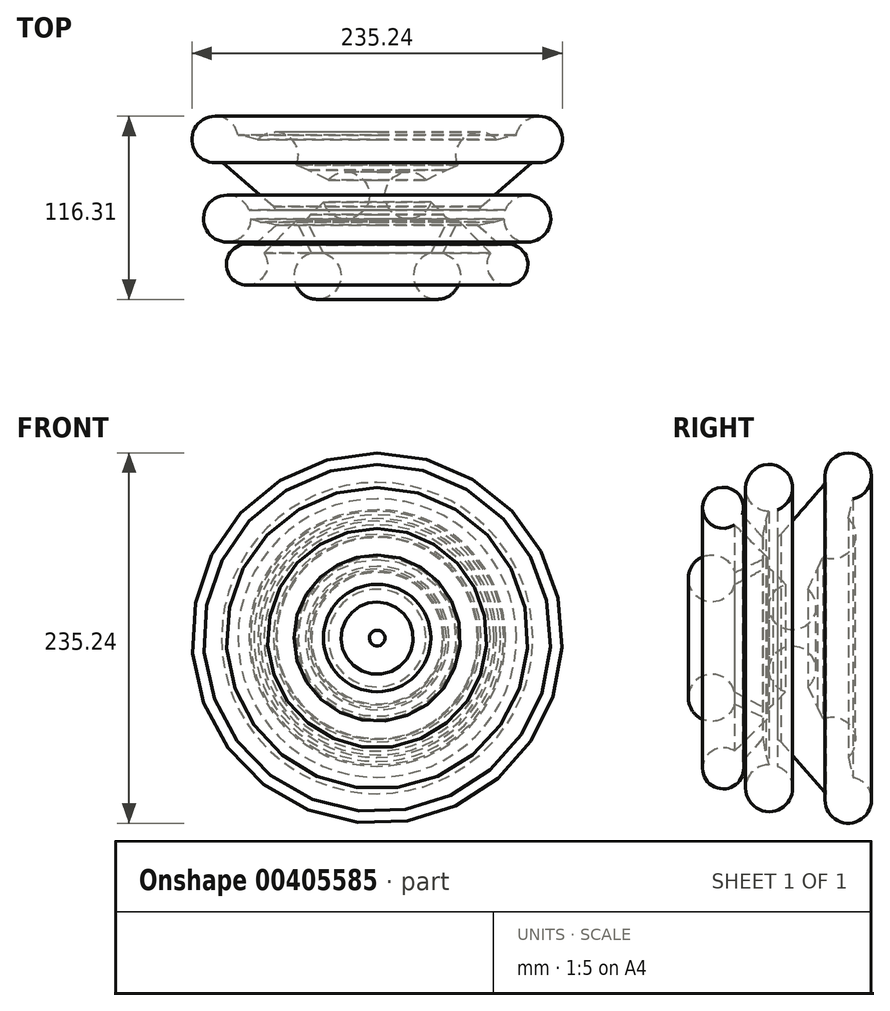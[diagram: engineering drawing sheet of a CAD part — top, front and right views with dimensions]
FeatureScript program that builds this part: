
annotation { "Feature Type Name" : "Feature", "Feature Type Description" : "" }
export const myFeature = defineFeature(function(context is Context, id is Id, definition is map)
    precondition{}
    {
        {
            var Q0;
            Q0=qCreatedBy(makeId("Top.planeOp"),FACE);
            var sketch = newSketch(context, id + "F0", { "sketchPlane" : qUnion([Q0])});
            skCircle(sketch, "E0", {"center": v(0, 48.43) * mm, "radius": 14.9 * mm});
            skCircle(sketch, "E1", {"center": v(-45.12, 23.16) * mm, "radius": 14.86 * mm});
            skCircle(sketch, "E2", {"center": v(-27.07, -27.97) * mm, "radius": 14.93 * mm});
            skCircle(sketch, "E3", {"center": v(17.75, -20.76) * mm, "radius": 13.06 * mm});
            skCircle(sketch, "E4", {"center": v(30.38, 8.42) * mm, "radius": 14.91 * mm});
            skCircle(sketch, "E5", {"center": v(37.9, 58.65) * mm, "radius": 14.75 * mm});
            skEllipticalArc(sketch, "E6", {});
            skEllipticalArc(sketch, "E7", {});
            skEllipticalArc(sketch, "E8.trimOffspring", {});
            skEllipticalArc(sketch, "E9.trimOffspring", {});
            skLineSegment(sketch, "E10", {"start": v(-34.02, 33.04) * mm, "end": v(-21.06, 39.1) * mm});
            skPoint(sketch, "E10.endSnap0", {"position": v(-21.06, 27.67) * mm});
            skLineSegment(sketch, "E11", {"start": v(-21.06, 39.1) * mm, "end": v(-13.65, 42.47) * mm});
            skLineSegment(sketch, "E12", {"start": v(-13.65, 42.47) * mm, "end": v(-11.61, 39.1) * mm});
            skLineSegment(sketch, "E13", {"start": v(-11.61, 39.1) * mm, "end": v(-30.9, 27.44) * mm});
            skLineSegment(sketch, "E14", {"start": v(-30.9, 27.44) * mm, "end": v(-19.47, 19.73) * mm});
            skLineSegment(sketch, "E15", {"start": v(-30.9, 18.88) * mm, "end": v(-22.56, 10.83) * mm});
            skLineSegment(sketch, "E16", {"start": v(-19.47, 8) * mm, "end": v(-30.9, -13.54) * mm});
            skLineSegment(sketch, "E17", {"start": v(-23.25, -13.54) * mm, "end": v(-13.65, 7.26) * mm});
            skLineSegment(sketch, "E18", {"start": v(-13.65, 7.26) * mm, "end": v(6.86, -13.54) * mm});
            skLineSegment(sketch, "E19", {"start": v(13.37, -8.45) * mm, "end": v(0, 3.3) * mm});
            skLineSegment(sketch, "E20", {"start": v(9.3, 6.23) * mm, "end": v(15.47, 8.18) * mm});
            skLineSegment(sketch, "E21", {"start": v(16.48, 13.8) * mm, "end": v(-0.59, 13.8) * mm});
            skLineSegment(sketch, "E22", {"start": v(0.94, 15.99) * mm, "end": v(33.87, 44.46) * mm});
            skLineSegment(sketch, "E23", {"start": v(26.72, 49.03) * mm, "end": v(1.02, 22.5) * mm});
            skLineSegment(sketch, "E24", {"start": v(23.45, 61.6) * mm, "end": v(10.87, 58.61) * mm});
            skLineSegment(sketch, "E25", {"start": v(13.94, 53.68) * mm, "end": v(24.01, 53.68) * mm});
            skPoint(sketch, "E26.orphan", {"position": v(-1.58, 13.8) * mm});
            skPoint(sketch, "E27.orphan", {"position": v(0, 21.44) * mm});
            skLineSegment(sketch, "E28", {"start": v(0, 3.3) * mm, "end": v(-1.17, 4.33) * mm});
            skLineSegment(sketch, "E29", {"start": v(-1.17, 4.33) * mm, "end": v(9.3, 6.23) * mm});
            skLineSegment(sketch, "E30", {"start": v(-64.97, 73.4) * mm, "end": v(-64.97, -50.83) * mm});
            const initialGuessF0  = {"E6": [-0.01052763219922781, 0.016242632642388344, -0.9119214800801739, -0.41036473309531, 0.013193656166304833, 0.007958897557757515, 5.24737243767985, 1.4032411330413588], "E7": [-0.01052763219922781, 0.016242632642388344, 0.6774757114096869, -0.7355451450794429, 0.015539496063272316, 0.005070487958191671, 2.0201571546067063, 4.124258026299893], "E8.trimOffspring": [-0.01052763219922781, 0.016242632642388344, 0.6774757114096869, -0.7355451450794429, 0.015539496063272316, 0.005070487958191671, 5.1617498081965, 0.9826653727100997], "E9.trimOffspring": [-0.01052763219922781, 0.016242632642388344, -0.9119214800801739, -0.41036473309531, 0.013193656166304833, 0.007958897557757515, 2.105779784090057, 4.54483378663115]};
            skSetInitialGuess(sketch, initialGuessF0);
            skSolve(sketch);
        }
        {
            var Q0;
            {var subQ0=sQuery(id+"F0.wireOp",EDGE,"E2");var subQ1=makeQuery(id+"F0.imprint","INTERSECT",VERTEX,{"derivedFrom":[subQ0,sQuery(id+"F0.wireOp",EDGE,"E16")]});Q0=makeQuery(id+"F0.imprint","IMPRINT",FACE,{"disambiguationData":[TD([[makeQuery(id+"F0.imprint","IMPRINT",EDGE,{"disambiguationData":[TD([[subQ1,1.0]])],"derivedFrom":subQ0}),1.0]])]});}
            var Q1;
            {var subQ0=sQuery(id+"F0.wireOp",EDGE,"E3");var subQ1=makeQuery(id+"F0.imprint","INTERSECT",VERTEX,{"derivedFrom":[subQ0,sQuery(id+"F0.wireOp",EDGE,"E18")]});Q1=makeQuery(id+"F0.imprint","IMPRINT",FACE,{"disambiguationData":[TD([[makeQuery(id+"F0.imprint","IMPRINT",EDGE,{"disambiguationData":[TD([[subQ1,1.0]])],"derivedFrom":subQ0}),1.0]])]});}
            var Q2;
            {var subQ0=sQuery(id+"F0.wireOp",EDGE,"E4");var subQ1=makeQuery(id+"F0.imprint","INTERSECT",VERTEX,{"derivedFrom":[subQ0,sQuery(id+"F0.wireOp",EDGE,"E20")]});Q2=makeQuery(id+"F0.imprint","IMPRINT",FACE,{"disambiguationData":[TD([[makeQuery(id+"F0.imprint","IMPRINT",EDGE,{"disambiguationData":[TD([[subQ1,1.0]])],"derivedFrom":subQ0}),1.0]])]});}
            var Q3;
            {var subQ11=sQuery(id+"F0.wireOp",EDGE,"E7");Q3=makeQuery(id+"F0.imprint","IMPRINT",FACE,{"disambiguationData":[TD([[makeQuery(id+"F0.imprint","IMPRINT",EDGE,{"derivedFrom":subQ11}),1.0]])]});}
            var Q4;
            {var subQ0=sQuery(id+"F0.wireOp",EDGE,"E22");Q4=makeQuery(id+"F0.imprint","IMPRINT",FACE,{"disambiguationData":[TD([[makeQuery(id+"F0.imprint","IMPRINT",EDGE,{"derivedFrom":subQ0}),1.0]])]});}
            var Q5;
            {var subQ0=sQuery(id+"F0.wireOp",EDGE,"E16");Q5=makeQuery(id+"F0.imprint","IMPRINT",FACE,{"disambiguationData":[TD([[makeQuery(id+"F0.imprint","IMPRINT",EDGE,{"derivedFrom":subQ0}),1.0]])]});}
            var Q6;
            {var subQ0=sQuery(id+"F0.wireOp",EDGE,"E1");var subQ1=makeQuery(id+"F0.imprint","INTERSECT",VERTEX,{"derivedFrom":[subQ0,sQuery(id+"F0.wireOp",EDGE,"E10")]});Q6=makeQuery(id+"F0.imprint","IMPRINT",FACE,{"disambiguationData":[TD([[makeQuery(id+"F0.imprint","IMPRINT",EDGE,{"disambiguationData":[TD([[subQ1,-1.0]])],"derivedFrom":subQ0}),1.0]])]});}
            var Q7;
            {var subQ0=sQuery(id+"F0.wireOp",EDGE,"E5");var subQ1=makeQuery(id+"F0.imprint","INTERSECT",VERTEX,{"derivedFrom":[subQ0,sQuery(id+"F0.wireOp",EDGE,"E24")]});Q7=makeQuery(id+"F0.imprint","IMPRINT",FACE,{"disambiguationData":[TD([[makeQuery(id+"F0.imprint","IMPRINT",EDGE,{"disambiguationData":[TD([[subQ1,-1.0]])],"derivedFrom":subQ0}),1.0]])]});}
            var Q8;
            {var subQ1=sQuery(id+"F0.wireOp",EDGE,"E10");Q8=makeQuery(id+"F0.imprint","IMPRINT",FACE,{"disambiguationData":[TD([[makeQuery(id+"F0.imprint","IMPRINT",EDGE,{"derivedFrom":subQ1}),-1.0]])]});}
            var Q9;
            {var subQ0=sQuery(id+"F0.wireOp",EDGE,"E14");Q9=makeQuery(id+"F0.imprint","IMPRINT",FACE,{"disambiguationData":[TD([[makeQuery(id+"F0.imprint","IMPRINT",EDGE,{"derivedFrom":subQ0}),-1.0]])]});}
            var Q10;
            {var subQ0=sQuery(id+"F0.wireOp",EDGE,"E24");Q10=makeQuery(id+"F0.imprint","IMPRINT",FACE,{"disambiguationData":[TD([[makeQuery(id+"F0.imprint","IMPRINT",EDGE,{"derivedFrom":subQ0}),1.0]])]});}
            var Q11;
            {var subQ0=sQuery(id+"F0.wireOp",EDGE,"E18");Q11=makeQuery(id+"F0.imprint","IMPRINT",FACE,{"disambiguationData":[TD([[makeQuery(id+"F0.imprint","IMPRINT",EDGE,{"derivedFrom":subQ0}),1.0]])]});}
            var Q12;
            {var subQ0=sQuery(id+"F0.wireOp",EDGE,"E7");Q12=makeQuery(id+"F0.imprint","IMPRINT",FACE,{"disambiguationData":[TD([[makeQuery(id+"F0.imprint","IMPRINT",EDGE,{"derivedFrom":subQ0}),-1.0]])]});}
            var Q13;
            {var subQ5=sQuery(id+"F0.wireOp",EDGE,"E20");Q13=makeQuery(id+"F0.imprint","IMPRINT",FACE,{"disambiguationData":[TD([[makeQuery(id+"F0.imprint","IMPRINT",EDGE,{"derivedFrom":subQ5}),1.0]])]});}
            var Q14;
            {var subQ3=sQuery(id+"F0.wireOp",EDGE,"E12");Q14=makeQuery(id+"F0.imprint","IMPRINT",FACE,{"disambiguationData":[TD([[makeQuery(id+"F0.imprint","IMPRINT",EDGE,{"derivedFrom":subQ3}),1.0]])]});}
            var Q15;
            {var subQ0=sQuery(id+"F0.wireOp",EDGE,"E29");var subQ1=sQuery(id+"F0.wireOp",EDGE,"E8.trimOffspring");var subQ3=makeQuery(id+"F0.imprint","INTERSECT",VERTEX,{"derivedFrom":[subQ1,subQ0]});Q15=makeQuery(id+"F0.imprint","IMPRINT",FACE,{"disambiguationData":[TD([[makeQuery(id+"F0.imprint","IMPRINT",EDGE,{"disambiguationData":[TD([[subQ3,1.0]])],"derivedFrom":subQ1}),1.0]])]});}
            var Q16;
            {var subQ0=sQuery(id+"F0.wireOp",EDGE,"E12");Q16=makeQuery(id+"F0.imprint","IMPRINT",FACE,{"disambiguationData":[TD([[makeQuery(id+"F0.imprint","IMPRINT",EDGE,{"derivedFrom":subQ0}),-1.0]])]});}
            var Q17;
            Q17=sQuery(id+"F0.wireOp",EDGE,"E30");
            revolve(context, id + "F1", {"entities" : qUnion([Q0, Q1, Q2, Q3, Q4, Q5, Q6, Q7, Q8, Q9, Q10, Q11, Q12, Q13, Q14, Q15, Q16]), "axis" : qUnion([Q17]), "revolveType" : RevolveType.FULL});
        }
    });
